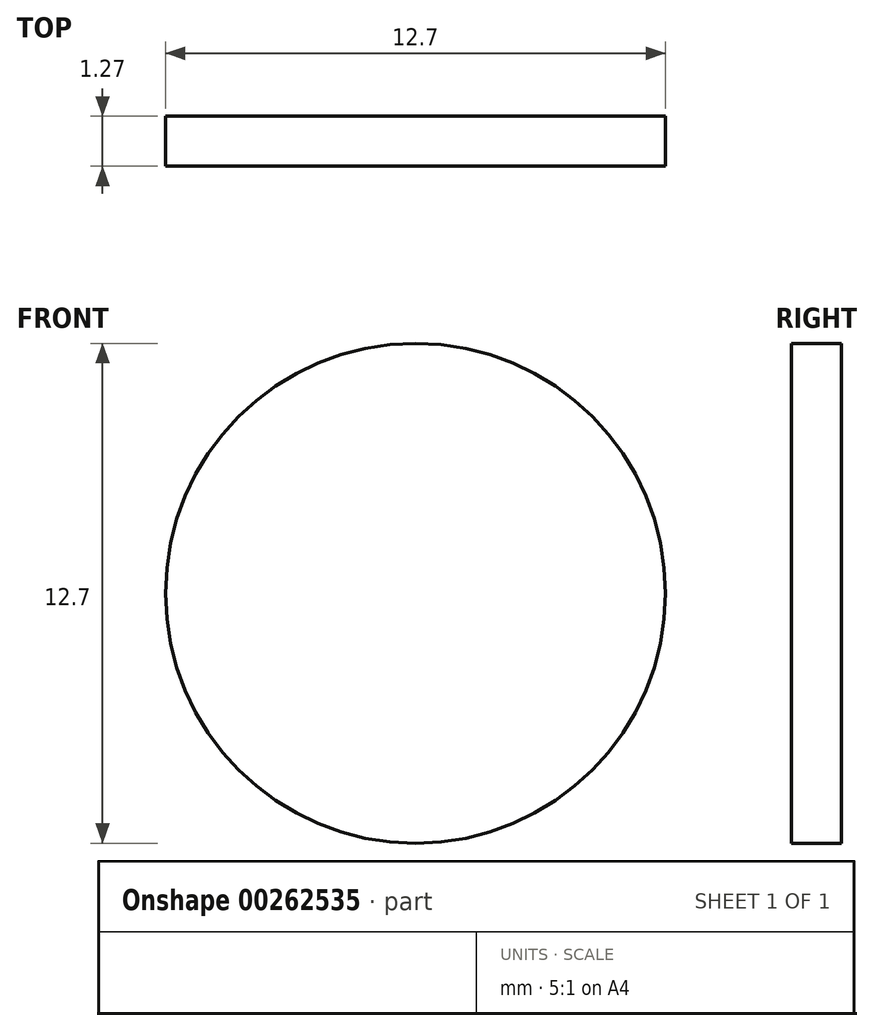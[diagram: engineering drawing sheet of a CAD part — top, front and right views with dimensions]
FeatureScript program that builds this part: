
annotation { "Feature Type Name" : "Feature", "Feature Type Description" : "" }
export const myFeature = defineFeature(function(context is Context, id is Id, definition is map)
    precondition{}
    {
        {
            var Q0;
            Q0=qCreatedBy(makeId("Front.planeOp"),FACE);
            var sketch = newSketch(context, id + "F0", { "sketchPlane" : qUnion([Q0])});
            skCircle(sketch, "E0", {"center": v(0, 0) * mm, "radius": 6.35 * mm});
            skSolve(sketch);
        }
        {
            var Q0;
            Q0 = qSketchRegion(id + "F0", true);
            extrude(context, id + "F1", {"entities" : qUnion([Q0]), "depth" : 1.27 * mm});
        }
    });
